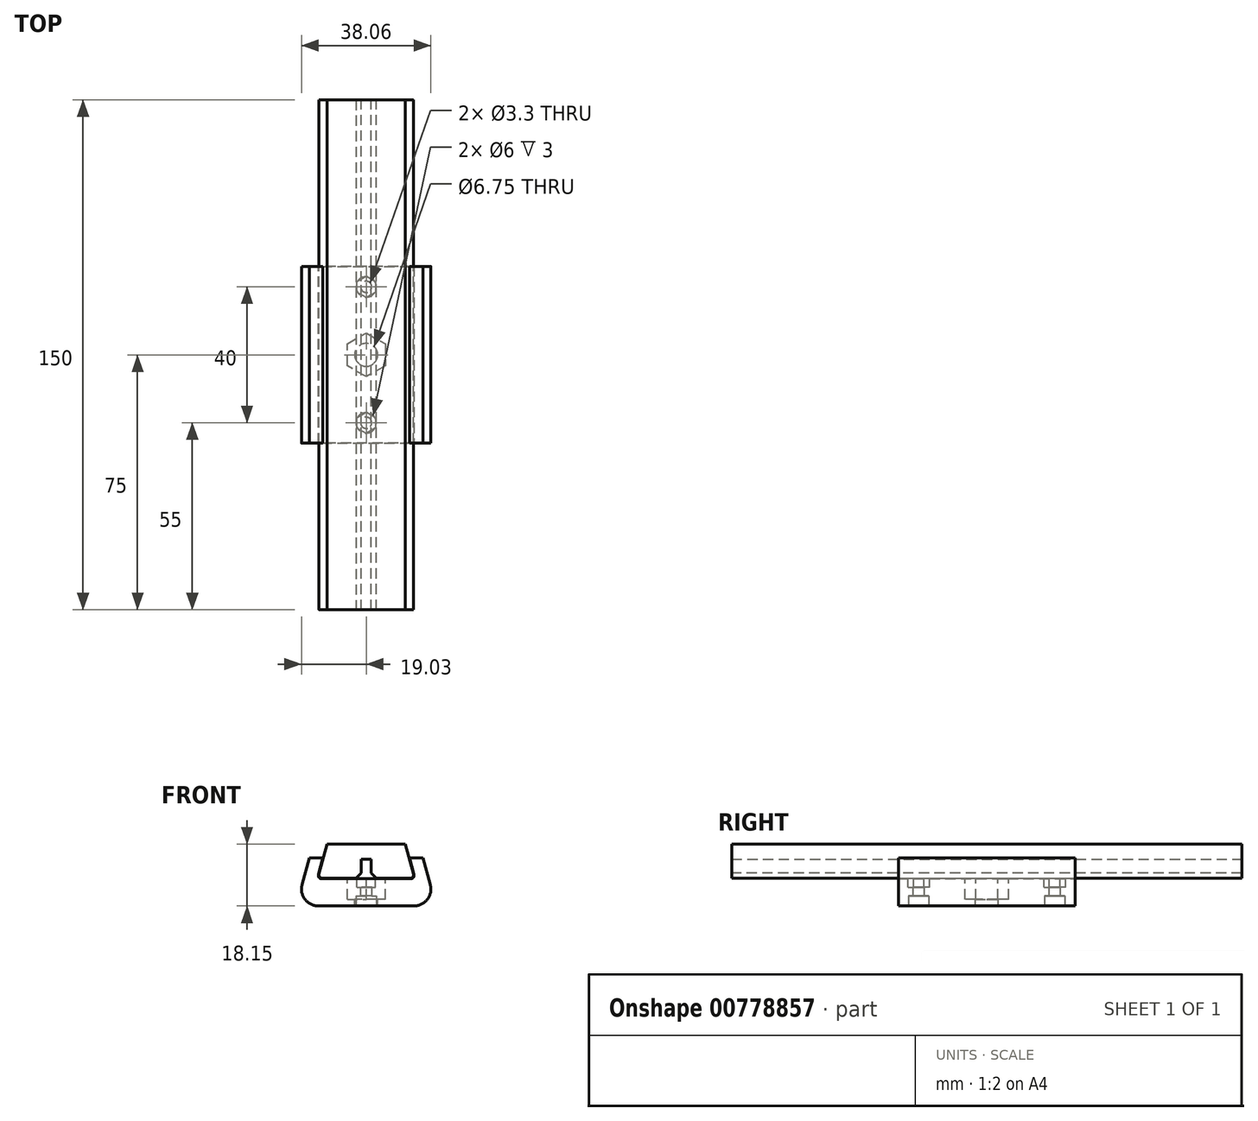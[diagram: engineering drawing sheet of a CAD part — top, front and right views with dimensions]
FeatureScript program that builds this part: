
annotation { "Feature Type Name" : "Feature", "Feature Type Description" : "" }
export const myFeature = defineFeature(function(context is Context, id is Id, definition is map)
    precondition{}
    {
        {
            var Q0;
            Q0=qCreatedBy(makeId("Front.planeOp"),FACE);
            var sketch = newSketch(context, id + "F0", { "sketchPlane" : qUnion([Q0])});
            skLineSegment(sketch, "E0", {"start": v(0, 5.66) * mm, "end": v(1.5, 5.66) * mm});
            skLineSegment(sketch, "E1", {"start": v(1.5, 5.66) * mm, "end": v(1.5, 0) * mm});
            skLineSegment(sketch, "E2", {"start": v(1.5, 0) * mm, "end": v(14.2, 0) * mm});
            skLineSegment(sketch, "E3", {"start": v(14.2, 0) * mm, "end": v(11.5, 10) * mm});
            skLineSegment(sketch, "E4", {"start": v(11.5, 10) * mm, "end": v(0, 10) * mm});
            skLineSegment(sketch, "E5.MirrorCS", {"start": v(-11.5, 10) * mm, "end": v(0, 10) * mm});
            skLineSegment(sketch, "E6.MirrorCS", {"start": v(-14.2, 0) * mm, "end": v(-11.5, 10) * mm});
            skLineSegment(sketch, "E7.MirrorCS", {"start": v(-1.5, 0) * mm, "end": v(-14.2, 0) * mm});
            skLineSegment(sketch, "E8.MirrorCS", {"start": v(-1.5, 5.66) * mm, "end": v(-1.5, 0) * mm});
            skLineSegment(sketch, "E9.MirrorCS", {"start": v(0, 5.66) * mm, "end": v(-1.5, 5.66) * mm});
            skLineSegment(sketch, "E10", {"start": v(0, -8.15) * mm, "end": v(20.56, -8.15) * mm});
            skLineSegment(sketch, "E11", {"start": v(20.56, -8.15) * mm, "end": v(16.74, 6) * mm});
            skLineSegment(sketch, "E12", {"start": v(16.74, 6) * mm, "end": v(12.74, 6) * mm});
            skLineSegment(sketch, "E13.0", {"start": v(14.4, -0.15) * mm, "end": v(12.74, 6) * mm});
            skLineSegment(sketch, "E13.1", {"start": v(2.07, -0.15) * mm, "end": v(14.4, -0.15) * mm});
            skLineSegment(sketch, "E14", {"start": v(2.07, -0.15) * mm, "end": v(0, -0.15) * mm});
            skLineSegment(sketch, "E15.MirrorCS", {"start": v(-2.07, -0.15) * mm, "end": v(0, -0.15) * mm});
            skLineSegment(sketch, "E16.MirrorCS", {"start": v(-2.07, -0.15) * mm, "end": v(-14.4, -0.15) * mm});
            skLineSegment(sketch, "E17.MirrorCS", {"start": v(0, -8.15) * mm, "end": v(-20.56, -8.15) * mm});
            skLineSegment(sketch, "E18.MirrorCS", {"start": v(-20.56, -8.15) * mm, "end": v(-16.74, 6) * mm});
            skLineSegment(sketch, "E19.MirrorCS", {"start": v(-16.74, 6) * mm, "end": v(-12.74, 6) * mm});
            skLineSegment(sketch, "E20.MirrorCS", {"start": v(-14.4, -0.15) * mm, "end": v(-12.74, 6) * mm});
            skSolve(sketch);
        }
        {
            var Q0;
            Q0=makeQuery(id+"F0.imprint","IMPRINT",FACE,{"disambiguationData":[TD([[makeQuery(id+"F0.imprint","IMPRINT",EDGE,{"derivedFrom":sQuery(id+"F0.wireOp",EDGE,"E0")}),1.0]])]});
            extrude(context, id + "F1", {"entities" : qUnion([Q0]), "depth" : 150 * mm, "offsetDistance" : 25 * mm, "symmetric" : true});
        }
        {
            var Q0;
            Q0=makeQuery(id+"F0.imprint","IMPRINT",FACE,{"disambiguationData":[TD([[makeQuery(id+"F0.imprint","IMPRINT",EDGE,{"derivedFrom":sQuery(id+"F0.wireOp",EDGE,"E10")}),1.0]])]});
            extrude(context, id + "F2", {"entities" : qUnion([Q0]), "depth" : 52 * mm, "offsetDistance" : 25 * mm, "symmetric" : true});
        }
        {
            var Q0;
            Q0=makeQuery(id+"F2.opExtrude","SWEPT_FACE",FACE,{"disambiguationData":[OSD([sQuery(id+"F0.wireOp",EDGE,"E13.1"),sQuery(id+"F0.wireOp",EDGE,"E14"),sQuery(id+"F0.wireOp",EDGE,"E15.MirrorCS"),sQuery(id+"F0.wireOp",EDGE,"E16.MirrorCS")])]});
            var sketch = newSketch(context, id + "F3", { "sketchPlane" : qUnion([Q0])});
            skCircle(sketch, "E21.cCircle", {"center": v(0, 0) * mm, "radius": 5.59 * mm, "construction": true});
            skLineSegment(sketch, "E21.0", {"start": v(5.59, -3.22) * mm, "end": v(0, -6.45) * mm});
            skLineSegment(sketch, "E21.1", {"start": v(0, -6.45) * mm, "end": v(-5.59, -3.23) * mm});
            skLineSegment(sketch, "E21.2", {"start": v(-5.59, -3.23) * mm, "end": v(-5.59, 3.22) * mm});
            skLineSegment(sketch, "E21.3", {"start": v(-5.59, 3.22) * mm, "end": v(0, 6.45) * mm});
            skLineSegment(sketch, "E21.4", {"start": v(0, 6.45) * mm, "end": v(5.59, 3.23) * mm});
            skLineSegment(sketch, "E21.5", {"start": v(5.59, 3.22) * mm, "end": v(5.59, -3.22) * mm});
            skPoint(sketch, "E21.0.midPoint", {"position": v(2.8, -4.84) * mm});
            skCircle(sketch, "E22", {"center": v(0, 0) * mm, "radius": 3.38 * mm});
            skCircle(sketch, "E23", {"center": v(0, 20) * mm, "radius": 1.65 * mm});
            skCircle(sketch, "E24", {"center": v(0, -20) * mm, "radius": 1.65 * mm});
            skCircle(sketch, "E25.cCircle", {"center": v(0, -20) * mm, "radius": 2.73 * mm, "construction": true});
            skLineSegment(sketch, "E25.0", {"start": v(2.73, -18.43) * mm, "end": v(2.73, -21.57) * mm});
            skLineSegment(sketch, "E25.1", {"start": v(2.73, -21.57) * mm, "end": v(0, -23.15) * mm});
            skLineSegment(sketch, "E25.2", {"start": v(0, -23.15) * mm, "end": v(-2.73, -21.57) * mm});
            skLineSegment(sketch, "E25.3", {"start": v(-2.73, -21.57) * mm, "end": v(-2.73, -18.43) * mm});
            skLineSegment(sketch, "E25.4", {"start": v(-2.73, -18.43) * mm, "end": v(0, -16.85) * mm});
            skLineSegment(sketch, "E25.5", {"start": v(0, -16.85) * mm, "end": v(2.73, -18.42) * mm});
            skPoint(sketch, "E25.0.midPoint", {"position": v(2.73, -20) * mm});
            skCircle(sketch, "E26.cCircle", {"center": v(0, 20) * mm, "radius": 2.73 * mm, "construction": true});
            skLineSegment(sketch, "E26.0", {"start": v(0, 23.15) * mm, "end": v(2.73, 21.57) * mm});
            skLineSegment(sketch, "E26.1", {"start": v(2.73, 21.57) * mm, "end": v(2.73, 18.43) * mm});
            skLineSegment(sketch, "E26.2", {"start": v(2.73, 18.42) * mm, "end": v(0, 16.85) * mm});
            skLineSegment(sketch, "E26.3", {"start": v(0, 16.85) * mm, "end": v(-2.73, 18.43) * mm});
            skLineSegment(sketch, "E26.4", {"start": v(-2.73, 18.43) * mm, "end": v(-2.73, 21.58) * mm});
            skLineSegment(sketch, "E26.5", {"start": v(-2.73, 21.58) * mm, "end": v(0, 23.15) * mm});
            skPoint(sketch, "E26.0.midPoint", {"position": v(1.36, 22.36) * mm});
            skSolve(sketch);
        }
        {
            var Q0;
            Q0=makeQuery(id+"F3.imprint","IMPRINT",FACE,{"disambiguationData":[TD([[makeQuery(id+"F3.imprint","IMPRINT",EDGE,{"derivedFrom":sQuery(id+"F3.wireOp",EDGE,"E22")}),1.0]])]});
            var Q1;
            Q1=makeQuery(id+"F3.imprint","IMPRINT",FACE,{"disambiguationData":[TD([[makeQuery(id+"F3.imprint","IMPRINT",EDGE,{"derivedFrom":sQuery(id+"F3.wireOp",EDGE,"E23")}),1.0]])]});
            var Q2;
            Q2=makeQuery(id+"F3.imprint","IMPRINT",FACE,{"disambiguationData":[TD([[makeQuery(id+"F3.imprint","IMPRINT",EDGE,{"derivedFrom":sQuery(id+"F3.wireOp",EDGE,"E24")}),1.0]])]});
            extrude(context, id + "F4", {"entities" : qUnion([Q0, Q1, Q2]), "operationType" : NewBodyOperationType.REMOVE, "endBound" : BoundingType.THROUGH_ALL, "oppositeDirection" : true, "depth" : 25 * mm, "offsetDistance" : 25 * mm});
        }
        {
            var Q0;
            Q0=makeQuery(id+"F3.imprint","IMPRINT",FACE,{"disambiguationData":[TD([[makeQuery(id+"F3.imprint","IMPRINT",EDGE,{"derivedFrom":sQuery(id+"F3.wireOp",EDGE,"E21.0")}),-1.0]])]});
            extrude(context, id + "F5", {"entities" : qUnion([Q0]), "operationType" : NewBodyOperationType.REMOVE, "oppositeDirection" : true, "depth" : 6 * mm, "offsetDistance" : 25 * mm});
        }
        {
            var Q0;
            Q0=makeQuery(id+"F1.opExtrude","SWEPT_EDGE",EDGE,{"disambiguationData":[OSD([sQuery(id+"F0.wireOp",EDGE,"E7.MirrorCS"),sQuery(id+"F0.wireOp",EDGE,"E8.MirrorCS")])]});
            var Q1;
            Q1=makeQuery(id+"F1.opExtrude","SWEPT_EDGE",EDGE,{"disambiguationData":[OSD([sQuery(id+"F0.wireOp",EDGE,"E1"),sQuery(id+"F0.wireOp",EDGE,"E2")])]});
            chamfer(context, id + "F6", {"entities" : qUnion([Q0, Q1]), "width" : 1.5 * mm, "tangentPropagation" : true});
        }
        {
            var Q0;
            Q0=makeQuery(id+"F1.opExtrude","SWEPT_EDGE",EDGE,{"disambiguationData":[OSD([sQuery(id+"F0.wireOp",EDGE,"E2"),sQuery(id+"F0.wireOp",EDGE,"E3")])]});
            var Q1;
            Q1=makeQuery(id+"F1.opExtrude","SWEPT_EDGE",EDGE,{"disambiguationData":[OSD([sQuery(id+"F0.wireOp",EDGE,"E6.MirrorCS"),sQuery(id+"F0.wireOp",EDGE,"E7.MirrorCS")])]});
            var Q2;
            Q2=makeQuery(id+"F2.opExtrude","SWEPT_EDGE",EDGE,{"disambiguationData":[OSD([sQuery(id+"F0.wireOp",EDGE,"E16.MirrorCS"),sQuery(id+"F0.wireOp",EDGE,"E20.MirrorCS")])]});
            var Q3;
            Q3=makeQuery(id+"F2.opExtrude","SWEPT_EDGE",EDGE,{"disambiguationData":[OSD([sQuery(id+"F0.wireOp",EDGE,"E13.0"),sQuery(id+"F0.wireOp",EDGE,"E13.1")])]});
            fillet(context, id + "F7", {"entities" : qUnion([Q0, Q1, Q2, Q3]), "radius" : 1 * mm, "tangentPropagation" : true, "allowEdgeOverflow" : false});
        }
        {
            var Q0;
            Q0=makeQuery(id+"F2.opExtrude","SWEPT_EDGE",EDGE,{"disambiguationData":[OSD([sQuery(id+"F0.wireOp",EDGE,"E17.MirrorCS"),sQuery(id+"F0.wireOp",EDGE,"E18.MirrorCS")])]});
            var Q1;
            Q1=makeQuery(id+"F2.opExtrude","SWEPT_EDGE",EDGE,{"disambiguationData":[OSD([sQuery(id+"F0.wireOp",EDGE,"E10"),sQuery(id+"F0.wireOp",EDGE,"E11")])]});
            fillet(context, id + "F8", {"entities" : qUnion([Q0, Q1]), "radius" : 5 * mm, "tangentPropagation" : true, "allowEdgeOverflow" : false});
        }
        {
            var Q0;
            Q0=makeQuery(id+"F2.opExtrude","SWEPT_FACE",FACE,{"disambiguationData":[OSD([sQuery(id+"F0.wireOp",EDGE,"E10"),sQuery(id+"F0.wireOp",EDGE,"E17.MirrorCS")])]});
            var sketch = newSketch(context, id + "F9", { "sketchPlane" : qUnion([Q0])});
            skCircle(sketch, "E27", {"center": v(0, 20) * mm, "radius": 3 * mm});
            skCircle(sketch, "E28", {"center": v(0, -20) * mm, "radius": 3 * mm});
            skSolve(sketch);
        }
        {
            var Q0;
            Q0=makeQuery(id+"F9.imprint","IMPRINT",FACE,{"disambiguationData":[TD([[makeQuery(id+"F9.imprint","IMPRINT",EDGE,{"derivedFrom":sQuery(id+"F9.wireOp",EDGE,"E27")}),1.0]])]});
            var Q1;
            Q1=makeQuery(id+"F9.imprint","IMPRINT",FACE,{"disambiguationData":[TD([[makeQuery(id+"F9.imprint","IMPRINT",EDGE,{"derivedFrom":sQuery(id+"F9.wireOp",EDGE,"E28")}),1.0]])]});
            extrude(context, id + "F10", {"entities" : qUnion([Q0, Q1]), "operationType" : NewBodyOperationType.REMOVE, "oppositeDirection" : true, "depth" : 3 * mm, "offsetDistance" : 25 * mm});
        }
        {
            var Q0;
            Q0=makeQuery(id+"F3.imprint","IMPRINT",FACE,{"disambiguationData":[TD([[makeQuery(id+"F3.imprint","IMPRINT",EDGE,{"derivedFrom":sQuery(id+"F3.wireOp",EDGE,"E23")}),-1.0]])]});
            var Q1;
            Q1=makeQuery(id+"F3.imprint","IMPRINT",FACE,{"disambiguationData":[TD([[makeQuery(id+"F3.imprint","IMPRINT",EDGE,{"derivedFrom":sQuery(id+"F3.wireOp",EDGE,"E24")}),-1.0]])]});
            extrude(context, id + "F11", {"entities" : qUnion([Q0, Q1]), "operationType" : NewBodyOperationType.REMOVE, "surfaceOperationType" : NewSurfaceOperationType.ADD, "oppositeDirection" : true, "depth" : 2.5 * mm, "offsetDistance" : 25 * mm});
        }
    });
